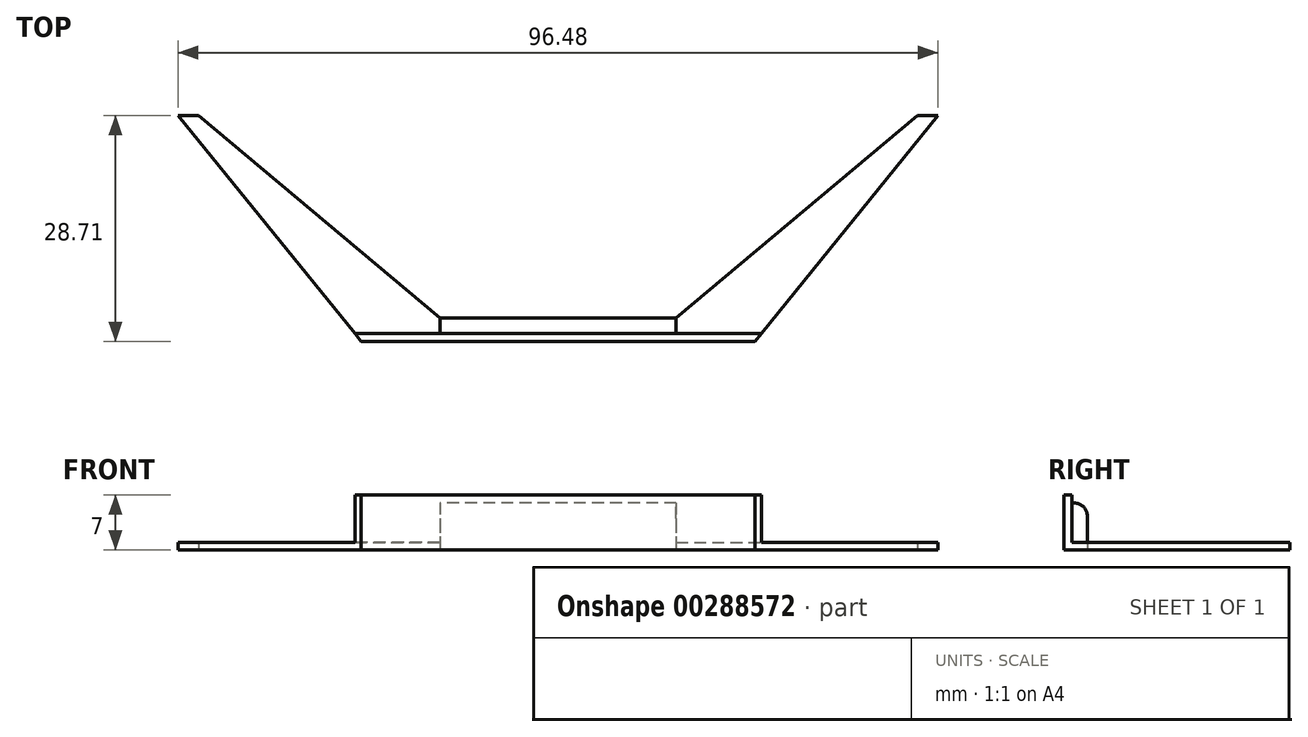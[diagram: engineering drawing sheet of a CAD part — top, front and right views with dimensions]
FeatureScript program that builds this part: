
annotation { "Feature Type Name" : "Feature", "Feature Type Description" : "" }
export const myFeature = defineFeature(function(context is Context, id is Id, definition is map)
    precondition{}
    {
        {
            var Q0;
            Q0=qCreatedBy(makeId("Top.planeOp"),FACE);
            var sketch = newSketch(context, id + "F0", { "sketchPlane" : qUnion([Q0])});
            skLineSegment(sketch, "E0", {"start": v(0, 0) * mm, "end": v(-15, 0) * mm});
            skLineSegment(sketch, "E1", {"start": v(-15, 0) * mm, "end": v(-45.64, 25.71) * mm});
            skLineSegment(sketch, "E2", {"start": v(-45.64, 25.71) * mm, "end": v(-48.24, 25.71) * mm});
            skLineSegment(sketch, "E3", {"start": v(-48.24, 25.71) * mm, "end": v(-25, -3) * mm});
            skLineSegment(sketch, "E4", {"start": v(-25, -3) * mm, "end": v(0, -3) * mm});
            skLineSegment(sketch, "E5.MirrorCS", {"start": v(0, 0) * mm, "end": v(15, 0) * mm});
            skLineSegment(sketch, "E6.MirrorCS", {"start": v(15, 0) * mm, "end": v(45.64, 25.71) * mm});
            skLineSegment(sketch, "E7.MirrorCS", {"start": v(45.64, 25.71) * mm, "end": v(48.24, 25.71) * mm});
            skLineSegment(sketch, "E8.MirrorCS", {"start": v(48.24, 25.71) * mm, "end": v(25, -3) * mm});
            skLineSegment(sketch, "E9.MirrorCS", {"start": v(25, -3) * mm, "end": v(0, -3) * mm});
            skSolve(sketch);
        }
        {
            var Q0;
            Q0=makeQuery(id+"F0.imprint","IMPRINT",FACE,{"disambiguationData":[TD([[makeQuery(id+"F0.imprint","IMPRINT",EDGE,{"derivedFrom":sQuery(id+"F0.wireOp",EDGE,"E0")}),1.0]])]});
            extrude(context, id + "F1", {"entities" : qUnion([Q0]), "depth" : 1 * mm});
        }
        {
            var Q0;
            Q0=makeQuery(id+"F1.opExtrude","CAP_FACE",FACE,{"disambiguationData":[OSD([sQuery(id+"F0.wireOp",EDGE,"E0"),sQuery(id+"F0.wireOp",EDGE,"E1"),sQuery(id+"F0.wireOp",EDGE,"E2"),sQuery(id+"F0.wireOp",EDGE,"E3"),sQuery(id+"F0.wireOp",EDGE,"E4"),sQuery(id+"F0.wireOp",EDGE,"E5.MirrorCS"),sQuery(id+"F0.wireOp",EDGE,"E6.MirrorCS"),sQuery(id+"F0.wireOp",EDGE,"E7.MirrorCS"),sQuery(id+"F0.wireOp",EDGE,"E8.MirrorCS"),sQuery(id+"F0.wireOp",EDGE,"E9.MirrorCS")])],"isStart":false});
            var sketch = newSketch(context, id + "F2", { "sketchPlane" : qUnion([Q0])});
            skLineSegment(sketch, "E10", {"start": v(-25.8, -2) * mm, "end": v(25.8, -2) * mm});
            skLineSegment(sketch, "E11", {"start": v(-15, 0) * mm, "end": v(-15, -2) * mm});
            skLineSegment(sketch, "E12", {"start": v(15, 0) * mm, "end": v(15, -2) * mm});
            skSolve(sketch);
        }
        {
            var Q0;
            {var subQ0=sQuery(id+"F2.wireOp",EDGE,"E10");Q0=makeQuery(id+"F2.imprint","IMPRINT",FACE,{"disambiguationData":[TD([[makeQuery(id+"F2.imprint","IMPRINT",EDGE,{"derivedFrom":subQ0}),-1.0]])]});}
            extrude(context, id + "F3", {"entities" : qUnion([Q0]), "operationType" : NewBodyOperationType.ADD, "depth" : 6 * mm});
        }
        {
            var Q0;
            Q0 = qSketchRegion(id + "F2", true);
            var Q1;
            {var subQ0=sQuery(id+"F2.wireOp",EDGE,"E11");Q1=makeQuery(id+"F2.imprint","IMPRINT",FACE,{"disambiguationData":[TD([[makeQuery(id+"F2.imprint","IMPRINT",EDGE,{"derivedFrom":subQ0}),1.0]])]});}
            extrude(context, id + "F4", {"entities" : qUnion([Q0, Q1]), "operationType" : NewBodyOperationType.ADD, "depth" : 5 * mm});
        }
        {
            var Q0;
            Q0=makeQuery(id+"F4.opExtrude","CAP_EDGE",EDGE,{"disambiguationData":[OSD([sQuery(id+"F0.wireOp",EDGE,"E0"),sQuery(id+"F0.wireOp",EDGE,"E5.MirrorCS")])],"isStart":false});
            fillet(context, id + "F5", {"entities" : qUnion([Q0]), "radius" : 2 * mm, "rho" : 0.5, "crossSection" : FilletCrossSection.CONIC, "allowEdgeOverflow" : false});
        }
    });
